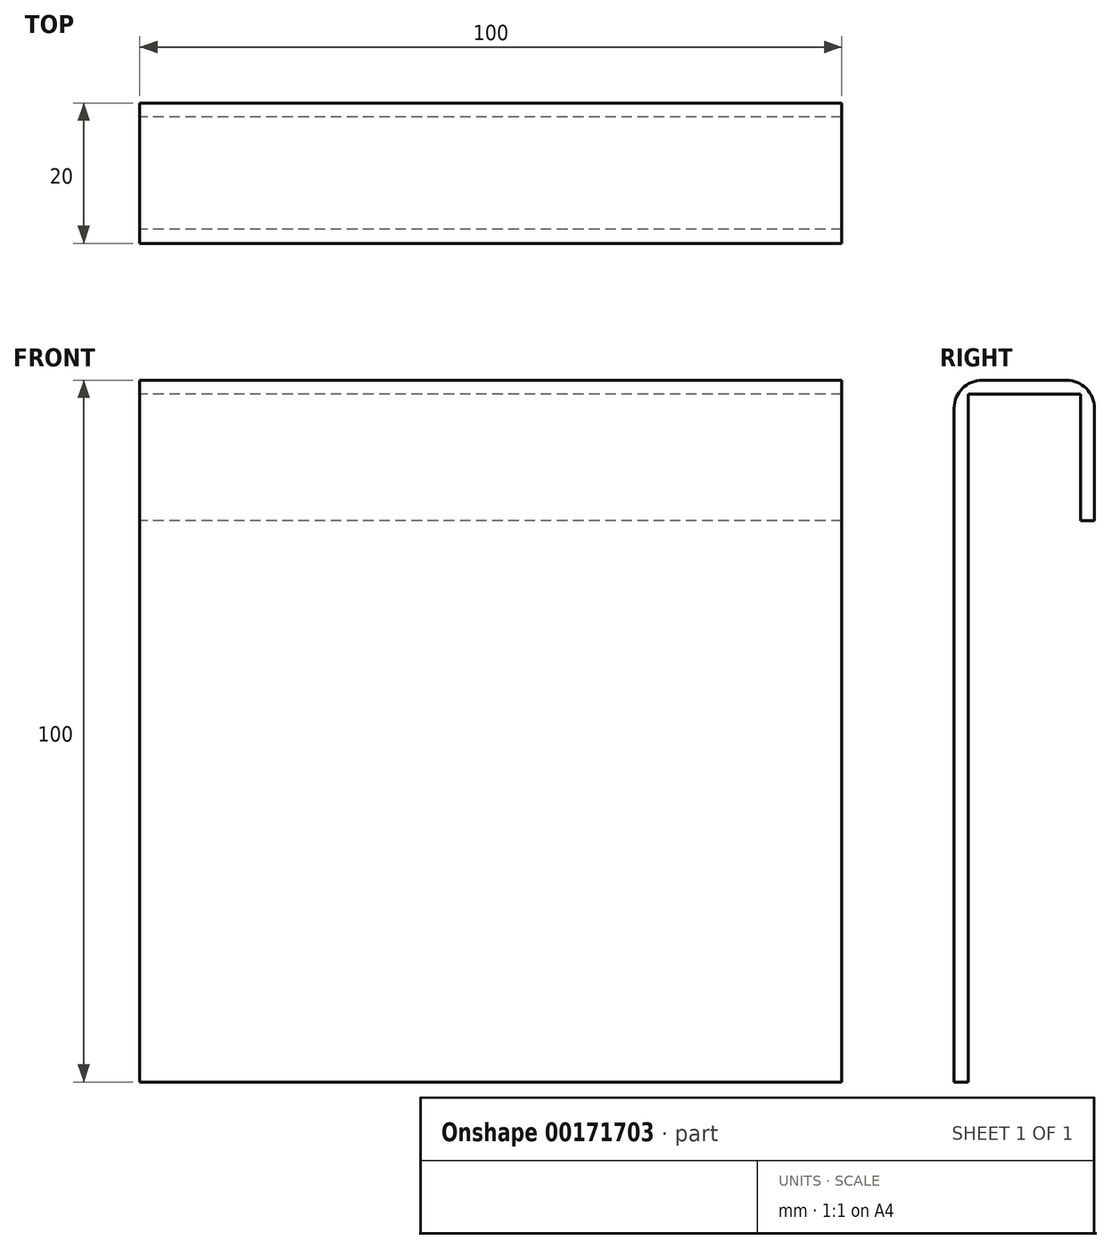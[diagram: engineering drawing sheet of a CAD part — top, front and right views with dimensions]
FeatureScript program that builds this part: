
annotation { "Feature Type Name" : "Feature", "Feature Type Description" : "" }
export const myFeature = defineFeature(function(context is Context, id is Id, definition is map)
    precondition{}
    {
        {
            var Q0;
            Q0=qCreatedBy(makeId("Right.planeOp"),FACE);
            var sketch = newSketch(context, id + "F0", { "sketchPlane" : qUnion([Q0])});
            skLineSegment(sketch, "E0.bottom", {"start": v(-6, 10) * mm, "end": v(6, 10) * mm});
            skLineSegment(sketch, "E0.left", {"start": v(-10, 6) * mm, "end": v(-10, -10) * mm});
            skLineSegment(sketch, "E0.right", {"start": v(10, 6) * mm, "end": v(10, -10) * mm});
            skPoint(sketch, "E0.middle", {"position": v(0, 0) * mm});
            skLineSegment(sketch, "E1", {"start": v(-10, -10) * mm, "end": v(-10, -90) * mm});
            skLineSegment(sketch, "E2.0", {"start": v(-8, -10) * mm, "end": v(-8, -90) * mm});
            skLineSegment(sketch, "E2.1", {"start": v(-8, 8) * mm, "end": v(-8, -10) * mm});
            skLineSegment(sketch, "E2.2", {"start": v(-8, 8) * mm, "end": v(8, 8) * mm});
            skLineSegment(sketch, "E2.3", {"start": v(8, 8) * mm, "end": v(8, -10) * mm});
            skPoint(sketch, "E3.visualSharp", {"position": v(-10, 10) * mm});
            skArc(sketch, "E3.filletArc", {"start": v(-6, 10) * mm, "mid": v(-8.83, 8.83) * mm, "end": v(-10, 6) * mm});
            skPoint(sketch, "E4.visualSharp", {"position": v(10, 10) * mm});
            skArc(sketch, "E4.filletArc", {"start": v(10, 6) * mm, "mid": v(8.83, 8.83) * mm, "end": v(6, 10) * mm});
            skLineSegment(sketch, "E5", {"start": v(8, -10) * mm, "end": v(10, -10) * mm});
            skLineSegment(sketch, "E6", {"start": v(-8, -90) * mm, "end": v(-10, -90) * mm});
            skSolve(sketch);
        }
        {
            var Q0;
            Q0 = qSketchRegion(id + "F0", true);
            extrude(context, id + "F1", {"entities" : qUnion([Q0]), "endBound" : BoundingType.SYMMETRIC, "depth" : 100 * mm});
        }
    });
